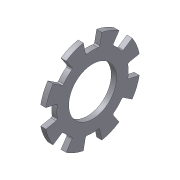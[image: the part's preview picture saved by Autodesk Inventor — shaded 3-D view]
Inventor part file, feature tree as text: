
AUTODESK INVENTOR PART (.ipt)
format: ipt  version: 2014 SP1 (Build 180222100, 222)  size: 133,120 bytes
history: native  units: mm (DEFAULTED — no unit token found)
features: sketch x2, extrude x1, pattern_circular x1
ambient origin geometry x8: Origin, YZ Plane, XZ Plane, XY Plane, X Axis, Y Axis, Z Axis, Center Point
bodies: Solid1 (feature_tree), Body (feature_tree)
feature tree (4):
  extrude  "Cut"  Depth=6.5024mm
  pattern_circular  "Cuts"  [2 undecoded]
  sketch  "Sketch1"  dims[d0=12.954mm d1=6.5024mm]
  sketch  "Sketch2"  dims[d2=0.7112mm d3=0.0mm d4=22.5deg d5=9.7282mm d6=0.7112mm d7=0.0mm d8=0.19431mm d9=80.0mm d11=360.0deg d12=0.0mm d13=0.0mm]
note: 2 required parameter values undecoded (feature->parameter linkage not recoverable at this tier; creation-order binding heuristic only, values carry confidence <= 0.55)
